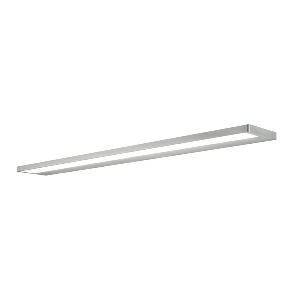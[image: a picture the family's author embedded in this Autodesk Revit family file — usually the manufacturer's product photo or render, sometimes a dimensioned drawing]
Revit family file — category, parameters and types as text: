
# Revit family: zera_wall_-_zew_6000_840_d_00812395_ca14
name_source: partatom
category: Lighting Fixtures
units: mm (PartAtom-declared; Revit-internal decimal feet)

## family parameters
Cut with Voids When Loaded = No
Host = Face
Light Source = No
Part Type = Normal
Room Calculation Point = No
Round Connector Dimension = Use Diameter
Shared = No

## types (1)
- ZERA.wall - ZEW 6000/840/D (1 x LED, 5600 lm, 4000K)
    Apparent Load = 40 VA
    Approval mark = CE
    CIE Flux Codes = 46 78 95 41 100
    Color Rendering = 80-89
    Color Temperature = 4000K
    Control Gear = Electronic ballast
    Default Elevation = 2000 mm  [stored 6.56168 ft]
    Description = ZEW 6000/840/D|Wall-mounted luminaire|light source:   Cold white   |work equipment: Adjustable electronic ballast, digital DALI|luminous flux: 5600 lm|light distribution: Direct/indirect|class of protection: I|technology: Continuously dimmable|mains lead: Connector 5 pin|glare control: Diffusor|special features: Asymmetric radiation, DALI Load 1x, DIN EN 60598-2-25, Suitable as emergency lighting|
    Frequency = 50 Hz, 60 Hz
    Height = 29 mm
    Lamp = 1 x LED
    Lamp Light Flux = 5600 lm
    Lamp count = 1
    Length = 1050 mm
    Luminous efficacy = 140 lm/W
    Manufacturer = Waldmann
    ModVariant = No
    Model = 00812395
    Mounting Place = Wall
    Mounting Type = Surface mounted
    Number of Poles = 1
    OnlyDefault = Yes
    Power Factor = 1
    Product Name = ZERA.wall - ZEW 6000/840/D
    Product group = Wall mounted Luminaire
    ProductGroupID = 20
    Protection Class = Protection class I
    Protection Degree = IP 20
    RLX_Detail_Level = 1
    RLX_Emergency_Light_Flux = 0 lm
    RLX_Emergency_Type = 0
    RLX_Emergency_Type_DB = No
    RlxData = <blob elided: 33257 chars, md5=5fbafec3>
    Socket = socket
    Standby Power = 0 W
    System Light Flux = 5600 lm
    System Power = 40 W
    Type Comments = Product without accessories
    Type Image = zera_40_w.jpg
    URL = http://relux.com
    VarID = ---
    Voltage = 230 V
    Voltage Range = 220-240 V
    Weight = 0.00 kg
    Width = 142 mm

note: [stored X ft] marks values corroborated as IEEE doubles in the binary element streams (Revit-internal decimal feet)

## geometry (parser evidence)
native form markers: Blend x4, Sweep x13
no freeform markers — native parametric forms only
